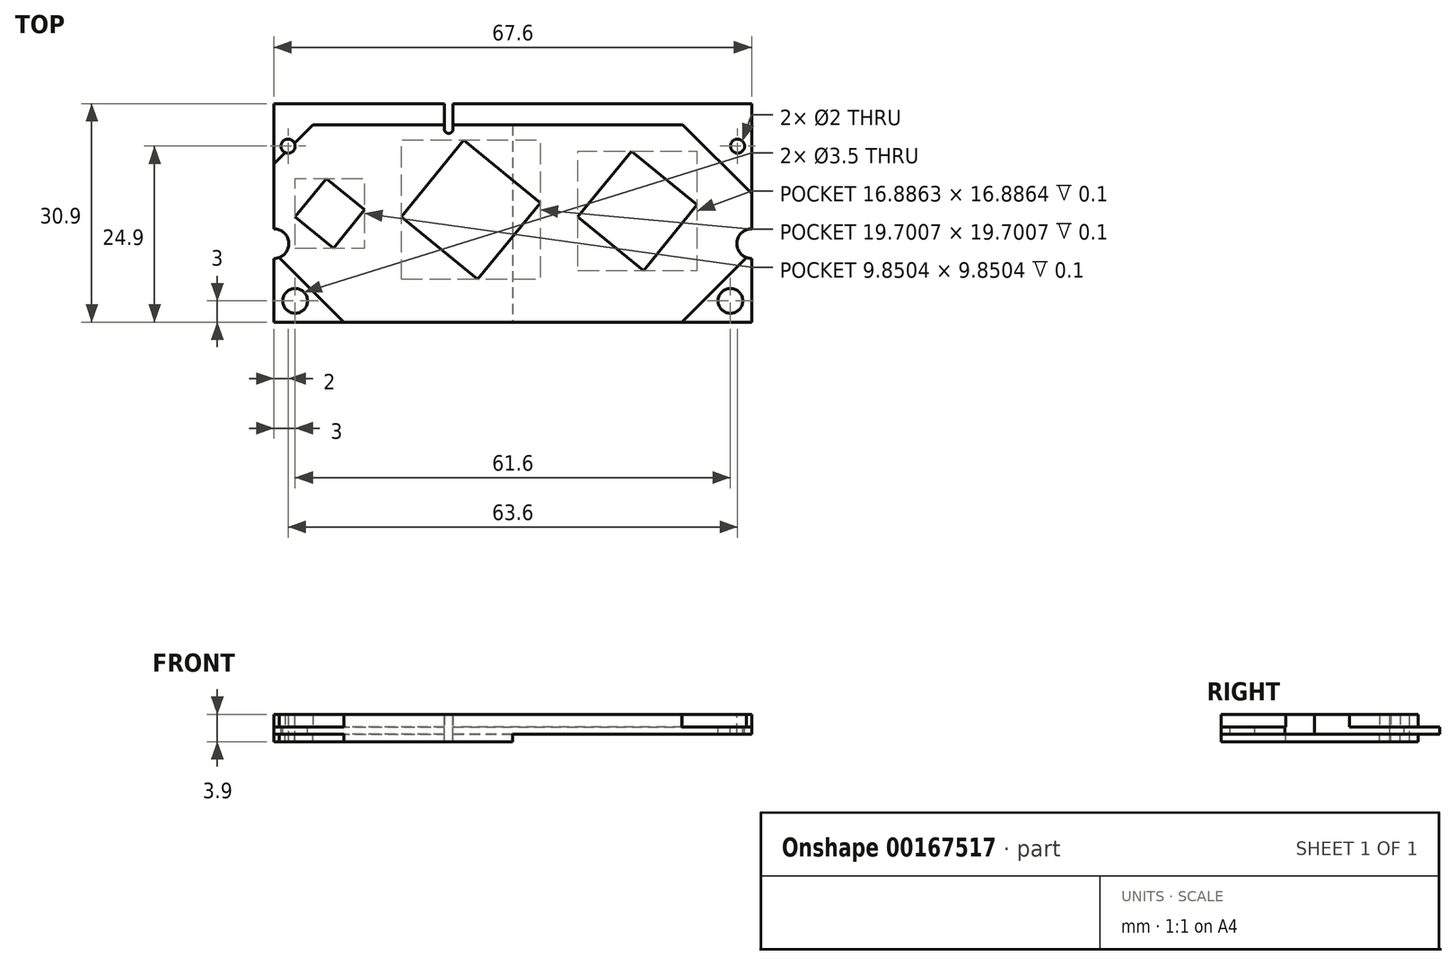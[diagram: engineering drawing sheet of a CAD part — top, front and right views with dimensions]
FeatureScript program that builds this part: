
annotation { "Feature Type Name" : "Feature", "Feature Type Description" : "" }
export const myFeature = defineFeature(function(context is Context, id is Id, definition is map)
    precondition{}
    {
        {
            var Q0;
            Q0=qCreatedBy(makeId("Top.planeOp"),FACE);
            var sketch = newSketch(context, id + "F0", { "sketchPlane" : qUnion([Q0])});
            skLineSegment(sketch, "E0", {"start": v(0, 0) * mm, "end": v(24.1, 0) * mm});
            skLineSegment(sketch, "E1", {"start": v(67.6, 0) * mm, "end": v(67.6, -17.7) * mm});
            skLineSegment(sketch, "E2", {"start": v(67.6, -30.9) * mm, "end": v(0, -30.9) * mm});
            skLineSegment(sketch, "E3", {"start": v(0, -30.9) * mm, "end": v(0, -21.9) * mm});
            skLineSegment(sketch, "E4", {"start": v(24.1, 0) * mm, "end": v(24.1, -3.58) * mm});
            skLineSegment(sketch, "E5", {"start": v(25.35, 0) * mm, "end": v(25.35, -3.58) * mm});
            skArc(sketch, "E6", {"start": v(24.1, -3.58) * mm, "mid": v(24.73, -4.2) * mm, "end": v(25.35, -3.58) * mm});
            skLineSegment(sketch, "E7.trimOffspring", {"start": v(25.35, 0) * mm, "end": v(67.6, 0) * mm});
            skArc(sketch, "E8", {"start": v(0, -21.9) * mm, "mid": v(2.1, -19.8) * mm, "end": v(0, -17.7) * mm});
            skLineSegment(sketch, "E9.trimOffspring", {"start": v(0, -17.7) * mm, "end": v(0, 0) * mm});
            skCircle(sketch, "E10", {"center": v(2, -6) * mm, "radius": 1 * mm});
            skCircle(sketch, "E11", {"center": v(3, -27.9) * mm, "radius": 1.75 * mm});
            skLineSegment(sketch, "E12", {"start": v(33.8, 0) * mm, "end": v(33.8, -30.9) * mm});
            skCircle(sketch, "E13.0.MirrorC", {"center": v(65.6, -6) * mm, "radius": 1 * mm});
            skCircle(sketch, "E14.0.MirrorC", {"center": v(64.6, -27.9) * mm, "radius": 1.75 * mm});
            skLineSegment(sketch, "E15", {"start": v(0, -19.8) * mm, "end": v(67.6, -19.8) * mm, "construction": true});
            skArc(sketch, "E16", {"start": v(67.6, -17.7) * mm, "mid": v(65.5, -19.8) * mm, "end": v(67.6, -21.9) * mm});
            skLineSegment(sketch, "E17.trimOffspring", {"start": v(67.6, -21.9) * mm, "end": v(67.6, -30.9) * mm});
            skLineSegment(sketch, "E18", {"start": v(67.6, -3) * mm, "end": v(25.35, -3) * mm});
            skLineSegment(sketch, "E19", {"start": v(24.1, -3) * mm, "end": v(0, -3) * mm});
            skLineSegment(sketch, "E20", {"start": v(0, -21) * mm, "end": v(9.9, -30.9) * mm});
            skLineSegment(sketch, "E21", {"start": v(67.6, -21) * mm, "end": v(57.7, -30.9) * mm});
            skLineSegment(sketch, "E22", {"start": v(8.49, 0) * mm, "end": v(0, -8.49) * mm});
            skLineSegment(sketch, "E23", {"start": v(54.87, 0) * mm, "end": v(67.6, -12.73) * mm});
            skSolve(sketch);
        }
        {
            var Q0;
            {var subQ1=sQuery(id+"F0.wireOp",EDGE,"E7.trimOffspring");Q0=makeQuery(id+"F0.imprint","IMPRINT",FACE,{"disambiguationData":[TD([[makeQuery(id+"F0.imprint","IMPRINT",EDGE,{"derivedFrom":subQ1}),-1.0]])]});}
            var Q1;
            Q1=makeQuery(id+"F0.imprint","IMPRINT",FACE,{"disambiguationData":[TD([[makeQuery(id+"F0.imprint","IMPRINT",EDGE,{"derivedFrom":sQuery(id+"F0.wireOp",EDGE,"E2")}),-1.0]])]});
            var Q2;
            {var subQ2=sQuery(id+"F0.wireOp",EDGE,"E0");Q2=makeQuery(id+"F0.imprint","IMPRINT",FACE,{"disambiguationData":[TD([[makeQuery(id+"F0.imprint","IMPRINT",EDGE,{"derivedFrom":subQ2}),-1.0]])]});}
            var Q3;
            {var subQ24=sQuery(id+"F0.wireOp",EDGE,"E6");Q3=makeQuery(id+"F0.imprint","IMPRINT",FACE,{"disambiguationData":[TD([[makeQuery(id+"F0.imprint","IMPRINT",EDGE,{"derivedFrom":subQ24}),-1.0]])]});}
            var Q4;
            {var subQ3=sQuery(id+"F0.wireOp",EDGE,"E9.trimOffspring");var subQ5=sQuery(id+"F0.wireOp",EDGE,"E19");var subQ8=makeQuery(id+"F0.imprint","INTERSECT",VERTEX,{"derivedFrom":[subQ3,subQ5]});Q4=makeQuery(id+"F0.imprint","IMPRINT",FACE,{"disambiguationData":[TD([[makeQuery(id+"F0.imprint","IMPRINT",EDGE,{"disambiguationData":[TD([[subQ8,1.0]])],"derivedFrom":subQ3}),-1.0]])]});}
            var Q5;
            {var subQ3=sQuery(id+"F0.wireOp",EDGE,"E1");var subQ5=sQuery(id+"F0.wireOp",EDGE,"E18");var subQ8=makeQuery(id+"F0.imprint","INTERSECT",VERTEX,{"derivedFrom":[subQ3,subQ5]});Q5=makeQuery(id+"F0.imprint","IMPRINT",FACE,{"disambiguationData":[TD([[makeQuery(id+"F0.imprint","IMPRINT",EDGE,{"disambiguationData":[TD([[subQ8,-1.0]])],"derivedFrom":subQ3}),-1.0]])]});}
            var Q6;
            {var subQ3=sQuery(id+"F0.wireOp",EDGE,"E1");var subQ6=sQuery(id+"F0.wireOp",EDGE,"E16");var subQ10=makeQuery(id+"F0.imprint","INTERSECT",VERTEX,{"derivedFrom":[subQ3,subQ6]});Q6=makeQuery(id+"F0.imprint","IMPRINT",FACE,{"disambiguationData":[TD([[makeQuery(id+"F0.imprint","IMPRINT",EDGE,{"disambiguationData":[TD([[subQ10,1.0]])],"derivedFrom":subQ3}),-1.0]])]});}
            extrude(context, id + "F1", {"entities" : qUnion([Q0, Q1, Q2, Q3, Q4, Q5, Q6]), "oppositeDirection" : true, "depth" : 1 * mm});
        }
        {
            var Q0;
            {var subQ24=sQuery(id+"F0.wireOp",EDGE,"E6");Q0=makeQuery(id+"F0.imprint","IMPRINT",FACE,{"disambiguationData":[TD([[makeQuery(id+"F0.imprint","IMPRINT",EDGE,{"derivedFrom":subQ24}),-1.0]])]});}
            extrude(context, id + "F2", {"entities" : qUnion([Q0]), "operationType" : NewBodyOperationType.ADD, "oppositeDirection" : true, "depth" : 2.1 * mm});
        }
        {
            var Q0;
            {var subQ24=sQuery(id+"F0.wireOp",EDGE,"E6");Q0=makeQuery(id+"F0.imprint","IMPRINT",FACE,{"disambiguationData":[TD([[makeQuery(id+"F0.imprint","IMPRINT",EDGE,{"derivedFrom":subQ24}),-1.0]])]});}
            var Q1;
            {var subQ3=sQuery(id+"F0.wireOp",EDGE,"E1");var subQ6=sQuery(id+"F0.wireOp",EDGE,"E16");var subQ10=makeQuery(id+"F0.imprint","INTERSECT",VERTEX,{"derivedFrom":[subQ3,subQ6]});Q1=makeQuery(id+"F0.imprint","IMPRINT",FACE,{"disambiguationData":[TD([[makeQuery(id+"F0.imprint","IMPRINT",EDGE,{"disambiguationData":[TD([[subQ10,1.0]])],"derivedFrom":subQ3}),-1.0]])]});}
            extrude(context, id + "F3", {"entities" : qUnion([Q0, Q1]), "operationType" : NewBodyOperationType.ADD, "depth" : 1.8 * mm});
        }
        {
            var Q0;
            Q0=qCreatedBy(makeId("Top.planeOp"),FACE);
            var sketch = newSketch(context, id + "F4", { "sketchPlane" : qUnion([Q0])});
            skLineSegment(sketch, "E24", {"start": v(26.87, -5.16) * mm, "end": v(18, -16) * mm});
            skLineSegment(sketch, "E25", {"start": v(18, -16) * mm, "end": v(28.84, -24.87) * mm});
            skLineSegment(sketch, "E26", {"start": v(28.84, -24.87) * mm, "end": v(37.7, -14.03) * mm});
            skLineSegment(sketch, "E27", {"start": v(37.7, -14.03) * mm, "end": v(26.87, -5.16) * mm});
            skLineSegment(sketch, "E28", {"start": v(12.85, -15.01) * mm, "end": v(7.43, -10.58) * mm});
            skLineSegment(sketch, "E29", {"start": v(7.43, -10.58) * mm, "end": v(3, -16) * mm});
            skLineSegment(sketch, "E30", {"start": v(3, -16) * mm, "end": v(8.42, -20.43) * mm});
            skLineSegment(sketch, "E31", {"start": v(8.42, -20.43) * mm, "end": v(12.85, -15.01) * mm});
            skLineSegment(sketch, "E32", {"start": v(59.89, -14.31) * mm, "end": v(50.6, -6.71) * mm});
            skLineSegment(sketch, "E33", {"start": v(50.6, -6.71) * mm, "end": v(43, -16) * mm});
            skLineSegment(sketch, "E34", {"start": v(43, -16) * mm, "end": v(52.29, -23.6) * mm});
            skLineSegment(sketch, "E35", {"start": v(52.29, -23.6) * mm, "end": v(59.89, -14.31) * mm});
            skSolve(sketch);
        }
        {
            var Q0;
            Q0=makeQuery(id+"F4.imprint","IMPRINT",FACE,{"disambiguationData":[TD([[makeQuery(id+"F4.imprint","IMPRINT",EDGE,{"derivedFrom":sQuery(id+"F4.wireOp",EDGE,"E28")}),1.0]])]});
            var Q1;
            Q1=makeQuery(id+"F4.imprint","IMPRINT",FACE,{"disambiguationData":[TD([[makeQuery(id+"F4.imprint","IMPRINT",EDGE,{"derivedFrom":sQuery(id+"F4.wireOp",EDGE,"E24")}),1.0]])]});
            var Q2;
            Q2=makeQuery(id+"F4.imprint","IMPRINT",FACE,{"disambiguationData":[TD([[makeQuery(id+"F4.imprint","IMPRINT",EDGE,{"derivedFrom":sQuery(id+"F4.wireOp",EDGE,"E32")}),1.0]])]});
            extrude(context, id + "F5", {"entities" : qUnion([Q0, Q1, Q2]), "operationType" : NewBodyOperationType.REMOVE, "depth" : 2 * mm, "hasSecondDirection" : true, "secondDirectionOppositeDirection" : false, "secondDirectionDepth" : 1.7 * mm});
        }
    });
